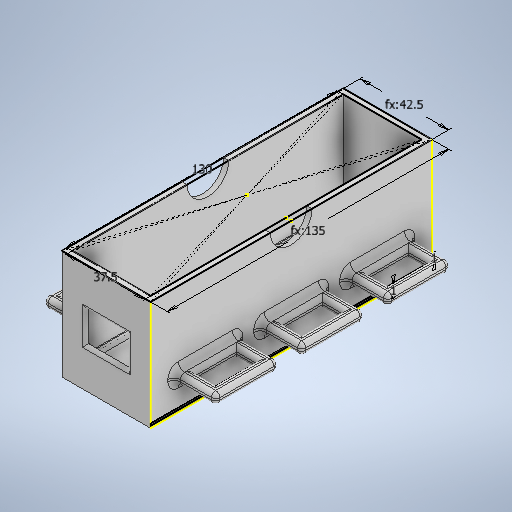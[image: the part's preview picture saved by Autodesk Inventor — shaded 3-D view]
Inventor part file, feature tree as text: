
AUTODESK INVENTOR PART (.ipt)
format: ipt  version: 2025 (Build 290162010, 162A)  size: 671,232 bytes
history: native  units: in
note: dims shown in document units (in); Inventor stores cm internally (conversion verified against a paired STEP export)
features: sketch x11, extrude x9, mirror x9, fillet x7, direct_edit x2, move_body x2
ambient origin geometry x8: Origin, YZ Plane, XZ Plane, XY Plane, X Axis, Y Axis, Z Axis, Center Point
bodies: Solid1 (feature_tree)
feature tree (40):
  sketch  "Sketch1"  dims[d0=1.4764in d1=5.1181in]
  extrude  "Extrusion1"  Depth=5.1181in
  extrude  "Extrusion2"  Depth=5.315in
  extrude  "Extrusion3"  Depth=1.9685in TaperAngle=0.0deg
  extrude  "Extrusion4"  Depth=0.1969in
  sketch  "Sketch4"  dims[d8=1.1811in d9=0.1969in]
  sketch  "Sketch5"  dims[d10=0.5167in d11=2.0669in d12=1.1811in d13=0.1969in d14=1.1811in d15=0.1969in]
  sketch  "Sketch6"  dims[d16=0.4429in d17=0.4429in]
  extrude  "Extrusion5"  Depth=2.0669in
  direct_edit  "Direct Edit1"
  fillet  "Fillet1"  Radius=1.1811in
  fillet  "Fillet2"  Radius=1.1811in
  fillet  "Face Fillet1"
  fillet  "Face Fillet2"
  fillet  "Face Fillet3"
  mirror  "Mirror4"
  mirror  "Mirror5"
  mirror  "Mirror6"
  mirror  "Mirror7"
  mirror  "Mirror8"
  sketch  "Sketch9"  dims[d25=0.3937in d26=0.7874in]
  extrude  "Extrusion7"  Depth=0.4429in
  extrude  "Extrusion8"  Depth=0.7874in TaperAngle=0.0deg
  fillet  "Fillet3"  Radius=0.7874in
  fillet  "Fillet4"  Radius=1.1811in
  extrude  "Extrusion9"  Depth=0.1969in
  mirror  "Mirror9"
  direct_edit  "Direct Edit2"
  mirror  "Mirror1"
  extrude  "Extrusion6"  Depth=0.7874in
  mirror  "Mirror2"
  mirror  "Mirror3"
  sketch  "Sketch2"  dims[d2=1.6732in d3=5.315in]
  sketch  "Sketch3"  dims[d4=2.0669in d5=0.0in d6=1.9685in d7=0.0in]
  sketch  "Sketch7"  dims[d18=0.4429in d19=0.7874in d20=0.0in d21=0.7874in d22=1.1811in]
  sketch  "Sketch8"  dims[d23=0.1969in d24=0.1969in]
  sketch  "Sketch10"  dims[d27=1.624in]
  sketch  "Sketch11"  dims[d28=0.3937in d29=0.7874in d30=0.3937in d31=0.7874in d32=0.7874in d33=0.0in d34=0.0394in d35=0.0394in d36=0.0394in d37=0.1181in d38=0.0394in d39=0.0in d40=0.0in d41=0.0in d42=0.0197in d43=0.0197in d44=0.0394in d45=0.0394in d46=0.3937in d47=0.0394in d48=0.0in d49=0.0787in d50=0.1181in d51=0.1181in d52=0.1181in d53=0.0787in d54=0.0in d55=0.0in d56=0.5906in d57=0.7087in d58=1.6732in d59=0.5413in d60=0.0984in d61=0.7874in d62=0.5906in d63=2.0669in d64=0.7382in d65=0.4429in d66=0.3937in d67=0.0in d68=0.3937in d69=0.0in d70=0.0591in d71=0.0591in d72=0.7874in d73=0.3937in d74=0.3937in d75=0.0in d76=2.2638in d77=5.315in d78=0.3937in d79=0.0in]
  move_body  "Move1"
  move_body  "Move2"
